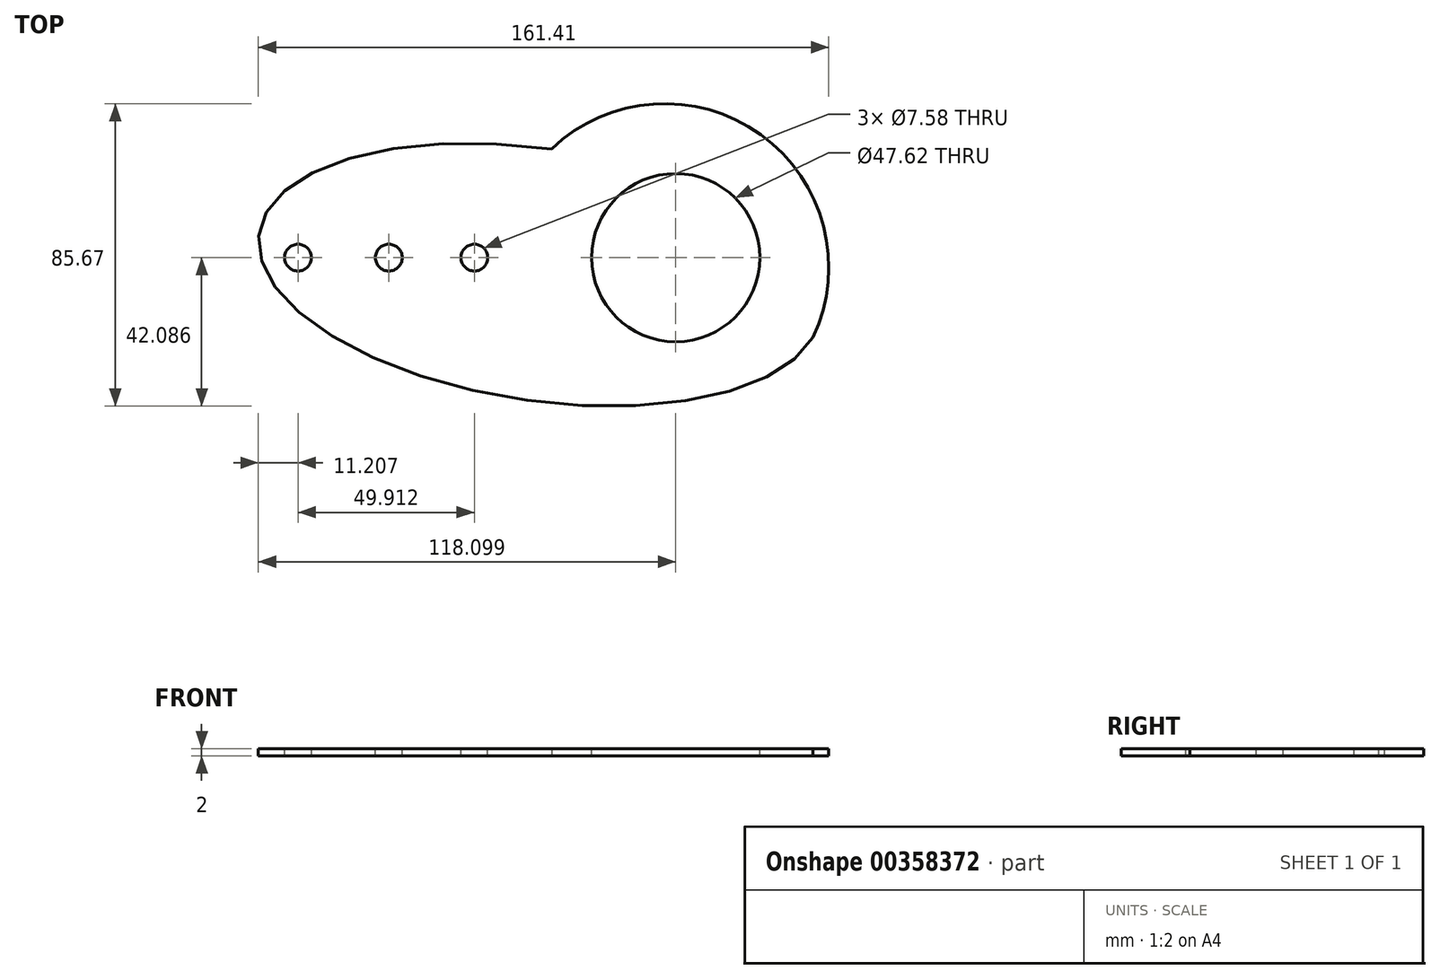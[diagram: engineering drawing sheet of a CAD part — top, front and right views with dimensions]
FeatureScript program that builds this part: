
annotation { "Feature Type Name" : "Feature", "Feature Type Description" : "" }
export const myFeature = defineFeature(function(context is Context, id is Id, definition is map)
    precondition{}
    {
        {
            var Q0;
            Q0=qCreatedBy(makeId("Top.planeOp"),FACE);
            var sketch = newSketch(context, id + "F0", { "sketchPlane" : qUnion([Q0])});
            skEllipticalArc(sketch, "E0", {});
            skArc(sketch, "E1", {"start": v(40.77, -11.01) * mm, "mid": v(25.94, 46.45) * mm, "end": v(-33.27, 42.4) * mm});
            const initialGuessF0  = {"E0": [-0.036548979580402374, 0.006794361863285307, 0.9892408338247206, -0.14629618140529702, 0.08034926837609735, 0.035719219722079934, 1.5952561053022674, 6.105784725868291]};
            skSetInitialGuess(sketch, initialGuessF0);
            skSolve(sketch);
        }
        {
            var Q0;
            Q0=makeQuery(id+"F0.imprint","IMPRINT",FACE,{"disambiguationData":[TD([[makeQuery(id+"F0.imprint","IMPRINT",EDGE,{"derivedFrom":sQuery(id+"F0.wireOp",EDGE,"E0")}),1.0]])]});
            extrude(context, id + "F1", {"entities" : qUnion([Q0]), "depth" : 2 * mm});
        }
        {
            var Q0;
            Q0=makeQuery(id+"F1.opExtrude","CAP_FACE",FACE,{"disambiguationData":[OSD([sQuery(id+"F0.wireOp",EDGE,"E0"),sQuery(id+"F0.wireOp",EDGE,"E1")])],"isStart":false});
            var sketch = newSketch(context, id + "F2", { "sketchPlane" : qUnion([Q0])});
            skCircle(sketch, "E2", {"center": v(1.89, 11.65) * mm, "radius": 23.81 * mm});
            skCircle(sketch, "E3", {"center": v(-105, 11.65) * mm, "radius": 3.8 * mm});
            skCircle(sketch, "E4", {"center": v(-79.3, 11.65) * mm, "radius": 3.8 * mm});
            skCircle(sketch, "E5", {"center": v(-55.1, 11.65) * mm, "radius": 3.8 * mm});
            skSolve(sketch);
        }
        {
            var Q0;
            Q0=makeQuery(id+"F2.imprint","IMPRINT",FACE,{"disambiguationData":[TD([[makeQuery(id+"F2.imprint","IMPRINT",EDGE,{"derivedFrom":sQuery(id+"F2.wireOp",EDGE,"E3")}),1.0]])]});
            var Q1;
            Q1=makeQuery(id+"F2.imprint","IMPRINT",FACE,{"disambiguationData":[TD([[makeQuery(id+"F2.imprint","IMPRINT",EDGE,{"derivedFrom":sQuery(id+"F2.wireOp",EDGE,"E4")}),1.0]])]});
            var Q2;
            Q2=makeQuery(id+"F2.imprint","IMPRINT",FACE,{"disambiguationData":[TD([[makeQuery(id+"F2.imprint","IMPRINT",EDGE,{"derivedFrom":sQuery(id+"F2.wireOp",EDGE,"E5")}),1.0]])]});
            var Q3;
            Q3=makeQuery(id+"F2.imprint","IMPRINT",FACE,{"disambiguationData":[TD([[makeQuery(id+"F2.imprint","IMPRINT",EDGE,{"derivedFrom":sQuery(id+"F2.wireOp",EDGE,"E2")}),1.0]])]});
            extrude(context, id + "F3", {"entities" : qUnion([Q0, Q1, Q2, Q3]), "operationType" : NewBodyOperationType.REMOVE, "endBound" : BoundingType.THROUGH_ALL, "oppositeDirection" : true, "depth" : 25.4 * mm});
        }
    });
